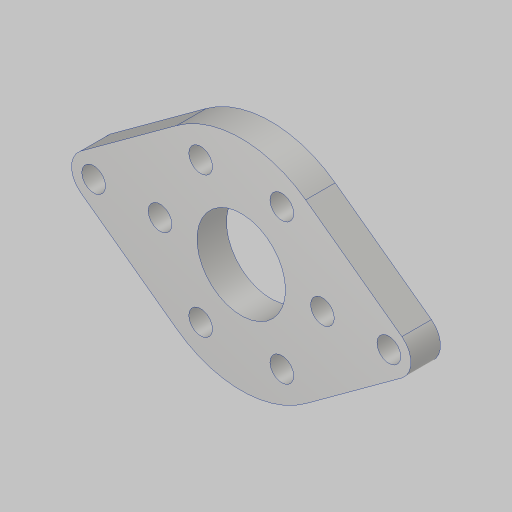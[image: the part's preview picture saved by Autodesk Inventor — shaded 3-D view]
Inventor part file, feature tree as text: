
AUTODESK INVENTOR PART (.ipt)
format: ipt  version: 2023.5 (Build 275446000, 446)  size: 141,312 bytes
history: native  units: in
note: dims shown in document units (in); Inventor stores cm internally (conversion verified against a paired STEP export)
features: sketch x1, extrude x1, hole x1
ambient origin geometry x8: Origin, YZ Plane, XZ Plane, XY Plane, X Axis, Y Axis, Z Axis, Center Point
bodies: Solid1 (feature_tree)
feature tree (3):
  sketch  "Sketch1"  dims[d0=0.375in d1=0.375in d2=2.5in d3=1.85in d4=0.75in d5=1.375in d6=2.3622in d8=360.0deg d11=0.25in d12=0.0in d13=0.201in d14=0.75in d15=0.385in d16=0.25in d17=0.5635in d18=1.0in d19=0.8108in]
  extrude  "Extrusion1"  Depth=0.375in
  hole  "Hole1"  [1 undecoded]
note: 1 required parameter value undecoded (feature->parameter linkage not recoverable at this tier; creation-order binding heuristic only, values carry confidence <= 0.55)
